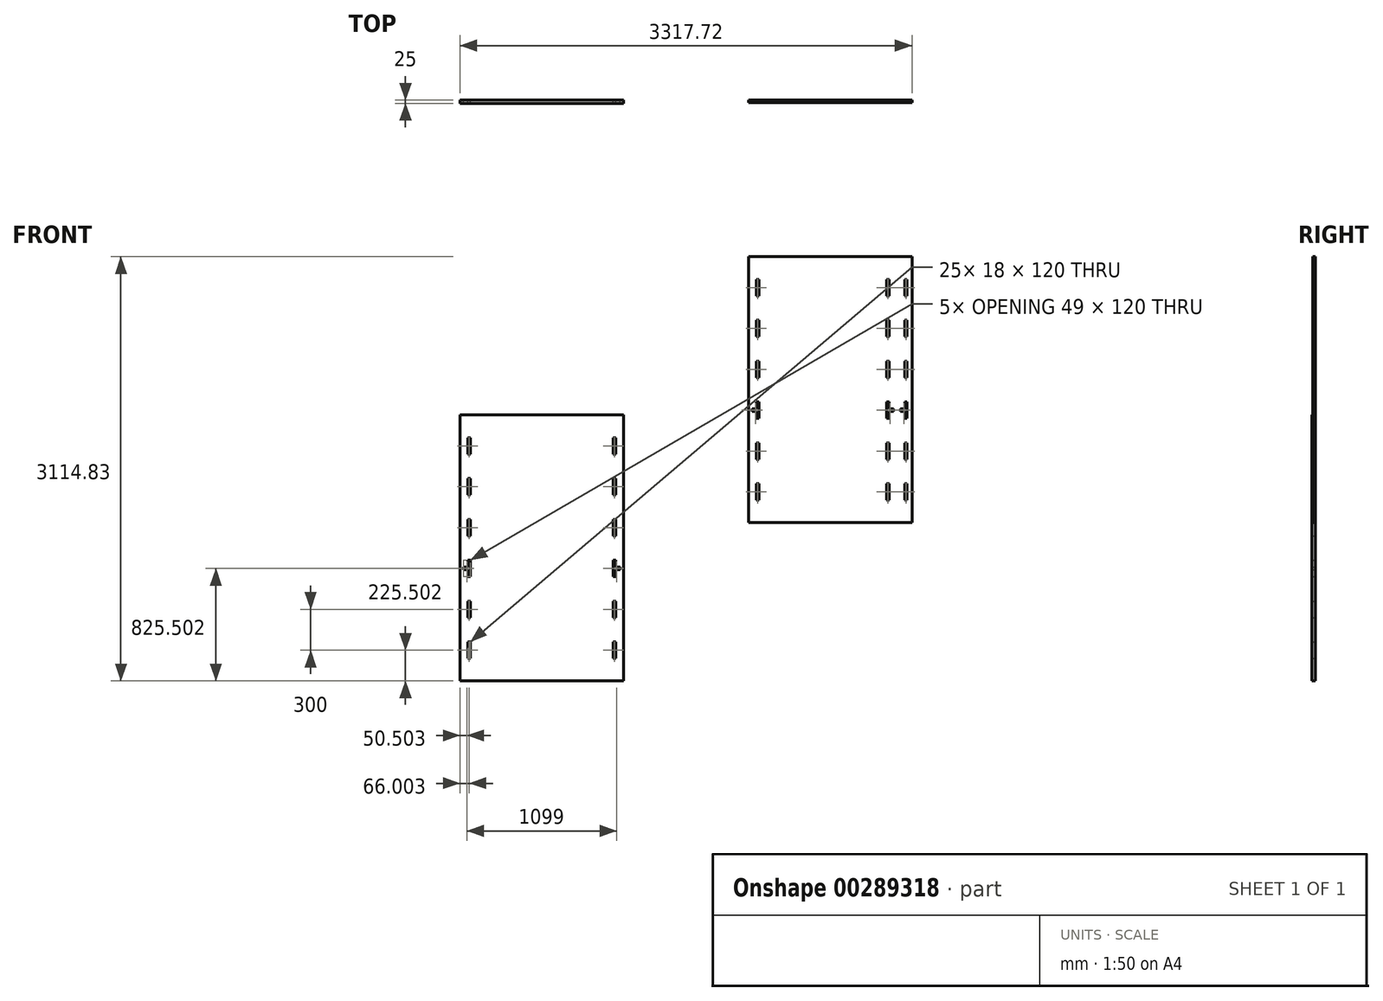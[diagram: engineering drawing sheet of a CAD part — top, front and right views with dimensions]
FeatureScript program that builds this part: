
annotation { "Feature Type Name" : "Feature", "Feature Type Description" : "" }
export const myFeature = defineFeature(function(context is Context, id is Id, definition is map)
    precondition{}
    {
        {
            var Q0;
            Q0=qCreatedBy(makeId("Front.planeOp"),FACE);
            var sketch = newSketch(context, id + "F0", { "sketchPlane" : qUnion([Q0])});
            skLineSegment(sketch, "E0.bottom", {"start": v(-15.59, 340) * mm, "end": v(15.41, 340) * mm});
            skLineSegment(sketch, "E0.top", {"start": v(-15.59, 322) * mm, "end": v(15.41, 322) * mm});
            skLineSegment(sketch, "E0.left", {"start": v(-15.59, 340) * mm, "end": v(-15.59, 322) * mm});
            skLineSegment(sketch, "E0.right", {"start": v(15.41, 340) * mm, "end": v(15.41, 322) * mm});
            skLineSegment(sketch, "E1.bottom", {"start": v(15.41, 391) * mm, "end": v(33.41, 391) * mm});
            skLineSegment(sketch, "E1.top", {"start": v(15.41, 271) * mm, "end": v(33.41, 271) * mm});
            skLineSegment(sketch, "E1.left", {"start": v(15.41, 391) * mm, "end": v(15.41, 271) * mm});
            skLineSegment(sketch, "E1.right", {"start": v(33.41, 391) * mm, "end": v(33.41, 271) * mm});
            skLineSegment(sketch, "E2", {"start": v(33.41, 331) * mm, "end": v(558.41, 331) * mm});
            skPoint(sketch, "E2.endSnap0", {"position": v(33.41, 331) * mm});
            skLineSegment(sketch, "E3", {"start": v(558.41, 331) * mm, "end": v(558.41, 369.03) * mm});
            skLineSegment(sketch, "E4.bottom", {"start": v(33.41, 571) * mm, "end": v(15.41, 571) * mm});
            skLineSegment(sketch, "E4.top", {"start": v(33.41, 691) * mm, "end": v(15.41, 691) * mm});
            skLineSegment(sketch, "E4.left", {"start": v(33.41, 571) * mm, "end": v(33.41, 691) * mm});
            skLineSegment(sketch, "E4.right", {"start": v(15.41, 571) * mm, "end": v(15.41, 691) * mm});
            skLineSegment(sketch, "E5.bottom", {"start": v(33.41, 871) * mm, "end": v(15.41, 871) * mm});
            skLineSegment(sketch, "E5.top", {"start": v(33.41, 991) * mm, "end": v(15.41, 991) * mm});
            skLineSegment(sketch, "E5.left", {"start": v(33.41, 871) * mm, "end": v(33.41, 991) * mm});
            skLineSegment(sketch, "E5.right", {"start": v(15.41, 871) * mm, "end": v(15.41, 991) * mm});
            skLineSegment(sketch, "E6.bottom", {"start": v(33.41, 1171) * mm, "end": v(15.41, 1171) * mm});
            skLineSegment(sketch, "E6.top", {"start": v(33.41, 1291) * mm, "end": v(15.41, 1291) * mm});
            skLineSegment(sketch, "E6.left", {"start": v(33.41, 1171) * mm, "end": v(33.41, 1291) * mm});
            skLineSegment(sketch, "E6.right", {"start": v(15.41, 1171) * mm, "end": v(15.41, 1291) * mm});
            skLineSegment(sketch, "E7", {"start": v(33.41, 1458) * mm, "end": v(15.41, 1458) * mm});
            skLineSegment(sketch, "E8", {"start": v(15.41, 1458) * mm, "end": v(-41.59, 1458) * mm});
            skLineSegment(sketch, "E9.bottom", {"start": v(15.41, 91) * mm, "end": v(33.41, 91) * mm});
            skLineSegment(sketch, "E9.top", {"start": v(15.41, -29) * mm, "end": v(33.41, -29) * mm});
            skLineSegment(sketch, "E9.left", {"start": v(15.41, 91) * mm, "end": v(15.41, -29) * mm});
            skLineSegment(sketch, "E9.right", {"start": v(33.41, 91) * mm, "end": v(33.41, -29) * mm});
            skLineSegment(sketch, "E10.bottom", {"start": v(15.41, -209) * mm, "end": v(33.41, -209) * mm});
            skLineSegment(sketch, "E10.top", {"start": v(15.41, -329) * mm, "end": v(33.41, -329) * mm});
            skLineSegment(sketch, "E10.left", {"start": v(15.41, -209) * mm, "end": v(15.41, -329) * mm});
            skLineSegment(sketch, "E10.right", {"start": v(33.41, -209) * mm, "end": v(33.41, -329) * mm});
            skLineSegment(sketch, "E11.bottom", {"start": v(15.41, -494.5) * mm, "end": v(33.41, -494.5) * mm});
            skLineSegment(sketch, "E12", {"start": v(69.41, -536.5) * mm, "end": v(69.41, -518.5) * mm});
            skLineSegment(sketch, "E13.MirrorCS", {"start": v(1101.41, 391) * mm, "end": v(1083.41, 391) * mm});
            skLineSegment(sketch, "E14.MirrorCS", {"start": v(1132.41, 322) * mm, "end": v(1101.41, 322) * mm});
            skLineSegment(sketch, "E15.MirrorCS", {"start": v(1101.41, -494.5) * mm, "end": v(1083.41, -494.5) * mm});
            skLineSegment(sketch, "E16.MirrorCS", {"start": v(1132.41, 340) * mm, "end": v(1101.41, 340) * mm});
            skLineSegment(sketch, "E17.MirrorCS", {"start": v(1101.41, -209) * mm, "end": v(1083.41, -209) * mm});
            skLineSegment(sketch, "E18.MirrorCS", {"start": v(1101.41, 271) * mm, "end": v(1083.41, 271) * mm});
            skLineSegment(sketch, "E19.MirrorCS", {"start": v(1101.41, 340) * mm, "end": v(1101.41, 322) * mm});
            skLineSegment(sketch, "E20.MirrorCS", {"start": v(1132.41, 340) * mm, "end": v(1132.41, 322) * mm});
            skLineSegment(sketch, "E21.MirrorCS", {"start": v(1101.41, -329) * mm, "end": v(1083.41, -329) * mm});
            skLineSegment(sketch, "E22.MirrorCS", {"start": v(1101.41, 391) * mm, "end": v(1101.41, 271) * mm});
            skLineSegment(sketch, "E23.MirrorCS", {"start": v(1083.41, 391) * mm, "end": v(1083.41, 271) * mm});
            skLineSegment(sketch, "E24.MirrorCS", {"start": v(1101.41, 91) * mm, "end": v(1101.41, -29) * mm});
            skLineSegment(sketch, "E25.MirrorCS", {"start": v(1101.41, 571) * mm, "end": v(1101.41, 691) * mm});
            skLineSegment(sketch, "E26.MirrorCS", {"start": v(1083.41, 871) * mm, "end": v(1101.41, 871) * mm});
            skLineSegment(sketch, "E27.MirrorCS", {"start": v(1083.41, 1291) * mm, "end": v(1101.41, 1291) * mm});
            skLineSegment(sketch, "E28.MirrorCS", {"start": v(1083.41, 691) * mm, "end": v(1101.41, 691) * mm});
            skLineSegment(sketch, "E29.MirrorCS", {"start": v(1101.41, 1458) * mm, "end": v(1158.41, 1458) * mm});
            skLineSegment(sketch, "E30.MirrorCS", {"start": v(1083.41, 991) * mm, "end": v(1101.41, 991) * mm});
            skLineSegment(sketch, "E31.MirrorCS", {"start": v(1101.41, -209) * mm, "end": v(1101.41, -329) * mm});
            skLineSegment(sketch, "E32.MirrorCS", {"start": v(1083.41, 571) * mm, "end": v(1101.41, 571) * mm});
            skLineSegment(sketch, "E33.MirrorCS", {"start": v(1083.41, 1458) * mm, "end": v(1101.41, 1458) * mm});
            skLineSegment(sketch, "E34.MirrorCS", {"start": v(1083.41, -209) * mm, "end": v(1083.41, -329) * mm});
            skLineSegment(sketch, "E35.MirrorCS", {"start": v(1101.41, 871) * mm, "end": v(1101.41, 991) * mm});
            skLineSegment(sketch, "E36.MirrorCS", {"start": v(1101.41, 91) * mm, "end": v(1083.41, 91) * mm});
            skLineSegment(sketch, "E37.MirrorCS", {"start": v(1101.41, 1171) * mm, "end": v(1101.41, 1291) * mm});
            skLineSegment(sketch, "E38.MirrorCS", {"start": v(1101.41, -29) * mm, "end": v(1083.41, -29) * mm});
            skLineSegment(sketch, "E39.MirrorCS", {"start": v(1083.41, 571) * mm, "end": v(1083.41, 691) * mm});
            skLineSegment(sketch, "E40.MirrorCS", {"start": v(1083.41, 1171) * mm, "end": v(1101.41, 1171) * mm});
            skLineSegment(sketch, "E41.MirrorCS", {"start": v(1083.41, 91) * mm, "end": v(1083.41, -29) * mm});
            skLineSegment(sketch, "E42.MirrorCS", {"start": v(1083.41, 1171) * mm, "end": v(1083.41, 1291) * mm});
            skLineSegment(sketch, "E43.MirrorCS", {"start": v(1083.41, 871) * mm, "end": v(1083.41, 991) * mm});
            skLineSegment(sketch, "E44.MirrorCS", {"start": v(1083.41, 331) * mm, "end": v(558.41, 331) * mm});
            skPoint(sketch, "E45.MirrorP", {"position": v(1083.41, 331) * mm});
            skLineSegment(sketch, "E46", {"start": v(1083.41, 1458) * mm, "end": v(33.41, 1458) * mm});
            skLineSegment(sketch, "E47", {"start": v(15.41, -494.5) * mm, "end": v(-41.59, -494.5) * mm});
            skLineSegment(sketch, "E48", {"start": v(33.41, -494.5) * mm, "end": v(558.41, -494.5) * mm});
            skLineSegment(sketch, "E49", {"start": v(558.41, -494.5) * mm, "end": v(1158.41, -494.5) * mm});
            skLineSegment(sketch, "E50", {"start": v(1158.41, 1458) * mm, "end": v(1158.41, -494.5) * mm});
            skLineSegment(sketch, "E51", {"start": v(-41.59, 1458) * mm, "end": v(-41.59, -494.5) * mm});
            skSolve(sketch);
        }
        {
            var Q0;
            {var subQ13=sQuery(id+"F0.wireOp",EDGE,"E0.bottom");Q0=makeQuery(id+"F0.imprint","IMPRINT",FACE,{"disambiguationData":[TD([[makeQuery(id+"F0.imprint","IMPRINT",EDGE,{"derivedFrom":subQ13}),1.0]])]});}
            extrude(context, id + "F1", {"entities" : qUnion([Q0]), "depth" : 25 * mm});
        }
        {
            var Q0;
            Q0=qCreatedBy(makeId("Front.planeOp"),FACE);
            var sketch = newSketch(context, id + "F2", { "sketchPlane" : qUnion([Q0])});
            skLineSegment(sketch, "E52.bottom", {"start": v(2102.13, 1502.33) * mm, "end": v(2133.13, 1502.33) * mm});
            skLineSegment(sketch, "E52.top", {"start": v(2102.13, 1484.33) * mm, "end": v(2133.13, 1484.33) * mm});
            skLineSegment(sketch, "E52.right", {"start": v(2133.13, 1502.33) * mm, "end": v(2133.13, 1484.33) * mm});
            skLineSegment(sketch, "E53.bottom", {"start": v(2133.13, 1553.33) * mm, "end": v(2151.13, 1553.33) * mm});
            skLineSegment(sketch, "E53.top", {"start": v(2133.13, 1433.33) * mm, "end": v(2151.13, 1433.33) * mm});
            skLineSegment(sketch, "E53.left", {"start": v(2133.13, 1553.33) * mm, "end": v(2133.13, 1433.33) * mm});
            skLineSegment(sketch, "E53.right", {"start": v(2151.13, 1553.33) * mm, "end": v(2151.13, 1433.33) * mm});
            skPoint(sketch, "E54.endSnap0", {"position": v(2151.13, 1493.33) * mm});
            skLineSegment(sketch, "E55.bottom", {"start": v(2151.13, 1733.33) * mm, "end": v(2133.13, 1733.33) * mm});
            skLineSegment(sketch, "E55.top", {"start": v(2151.13, 1853.33) * mm, "end": v(2133.13, 1853.33) * mm});
            skLineSegment(sketch, "E55.left", {"start": v(2151.13, 1733.33) * mm, "end": v(2151.13, 1853.33) * mm});
            skLineSegment(sketch, "E55.right", {"start": v(2133.13, 1733.33) * mm, "end": v(2133.13, 1853.33) * mm});
            skLineSegment(sketch, "E56.bottom", {"start": v(2151.13, 2033.33) * mm, "end": v(2133.13, 2033.33) * mm});
            skLineSegment(sketch, "E56.top", {"start": v(2151.13, 2153.33) * mm, "end": v(2133.13, 2153.33) * mm});
            skLineSegment(sketch, "E56.left", {"start": v(2151.13, 2033.33) * mm, "end": v(2151.13, 2153.33) * mm});
            skLineSegment(sketch, "E56.right", {"start": v(2133.13, 2033.33) * mm, "end": v(2133.13, 2153.33) * mm});
            skLineSegment(sketch, "E57.bottom", {"start": v(2151.13, 2333.33) * mm, "end": v(2133.13, 2333.33) * mm});
            skLineSegment(sketch, "E57.top", {"start": v(2151.13, 2453.33) * mm, "end": v(2133.13, 2453.33) * mm});
            skLineSegment(sketch, "E57.left", {"start": v(2151.13, 2333.33) * mm, "end": v(2151.13, 2453.33) * mm});
            skLineSegment(sketch, "E57.right", {"start": v(2133.13, 2333.33) * mm, "end": v(2133.13, 2453.33) * mm});
            skLineSegment(sketch, "E58.bottom", {"start": v(2133.13, 1253.33) * mm, "end": v(2151.13, 1253.33) * mm});
            skLineSegment(sketch, "E58.top", {"start": v(2133.13, 1133.33) * mm, "end": v(2151.13, 1133.33) * mm});
            skLineSegment(sketch, "E58.left", {"start": v(2133.13, 1253.33) * mm, "end": v(2133.13, 1133.33) * mm});
            skLineSegment(sketch, "E58.right", {"start": v(2151.13, 1253.33) * mm, "end": v(2151.13, 1133.33) * mm});
            skLineSegment(sketch, "E59.bottom", {"start": v(2133.13, 953.33) * mm, "end": v(2151.13, 953.33) * mm});
            skLineSegment(sketch, "E59.top", {"start": v(2133.13, 833.33) * mm, "end": v(2151.13, 833.33) * mm});
            skLineSegment(sketch, "E59.left", {"start": v(2133.13, 953.33) * mm, "end": v(2133.13, 833.33) * mm});
            skLineSegment(sketch, "E59.right", {"start": v(2151.13, 953.33) * mm, "end": v(2151.13, 833.33) * mm});
            skLineSegment(sketch, "E60.bottom", {"start": v(2133.13, 667.83) * mm, "end": v(2151.13, 667.83) * mm});
            skLineSegment(sketch, "E61", {"start": v(2102.13, 1502.33) * mm, "end": v(2102.13, 1484.33) * mm});
            skLineSegment(sketch, "E62", {"start": v(2151.13, 2620.33) * mm, "end": v(2133.13, 2620.33) * mm});
            skLineSegment(sketch, "E63", {"start": v(2133.13, 2620.33) * mm, "end": v(2076.13, 2620.33) * mm});
            skLineSegment(sketch, "E64.MirrorCS", {"start": v(3090.13, 2620.33) * mm, "end": v(3108.13, 2620.33) * mm});
            skLineSegment(sketch, "E65.MirrorCS", {"start": v(3090.13, 2453.33) * mm, "end": v(3108.13, 2453.33) * mm});
            skLineSegment(sketch, "E66.MirrorCS", {"start": v(3108.13, 2333.33) * mm, "end": v(3108.13, 2453.33) * mm});
            skLineSegment(sketch, "E67.MirrorCS", {"start": v(3090.13, 2333.33) * mm, "end": v(3108.13, 2333.33) * mm});
            skLineSegment(sketch, "E68.MirrorCS", {"start": v(3090.13, 2333.33) * mm, "end": v(3090.13, 2453.33) * mm});
            skLineSegment(sketch, "E69.MirrorCS", {"start": v(3090.13, 1733.33) * mm, "end": v(3108.13, 1733.33) * mm});
            skLineSegment(sketch, "E70.MirrorCS", {"start": v(3090.13, 2033.33) * mm, "end": v(3108.13, 2033.33) * mm});
            skLineSegment(sketch, "E71.MirrorCS", {"start": v(3090.13, 1853.33) * mm, "end": v(3108.13, 1853.33) * mm});
            skLineSegment(sketch, "E72.MirrorCS", {"start": v(3090.13, 2153.33) * mm, "end": v(3108.13, 2153.33) * mm});
            skLineSegment(sketch, "E73.MirrorCS", {"start": v(3108.13, 2033.33) * mm, "end": v(3108.13, 2153.33) * mm});
            skLineSegment(sketch, "E74.MirrorCS", {"start": v(3090.13, 1733.33) * mm, "end": v(3090.13, 1853.33) * mm});
            skLineSegment(sketch, "E75.MirrorCS", {"start": v(3108.13, 1733.33) * mm, "end": v(3108.13, 1853.33) * mm});
            skLineSegment(sketch, "E76.MirrorCS", {"start": v(3090.13, 2033.33) * mm, "end": v(3090.13, 2153.33) * mm});
            skLineSegment(sketch, "E77.MirrorCS", {"start": v(3108.13, 1433.33) * mm, "end": v(3090.13, 1433.33) * mm});
            skLineSegment(sketch, "E78.MirrorCS", {"start": v(3108.13, 1502.33) * mm, "end": v(3108.13, 1484.33) * mm});
            skLineSegment(sketch, "E79.MirrorCS", {"start": v(3108.13, 1553.33) * mm, "end": v(3090.13, 1553.33) * mm});
            skLineSegment(sketch, "E80.MirrorCS", {"start": v(3108.13, 1553.33) * mm, "end": v(3108.13, 1433.33) * mm});
            skLineSegment(sketch, "E81.MirrorCS", {"start": v(3108.13, 1133.33) * mm, "end": v(3090.13, 1133.33) * mm});
            skLineSegment(sketch, "E82.MirrorCS", {"start": v(3090.13, 1553.33) * mm, "end": v(3090.13, 1433.33) * mm});
            skLineSegment(sketch, "E83.MirrorCS", {"start": v(3108.13, 1253.33) * mm, "end": v(3090.13, 1253.33) * mm});
            skLineSegment(sketch, "E84.MirrorCS", {"start": v(3090.13, 1253.33) * mm, "end": v(3090.13, 1133.33) * mm});
            skPoint(sketch, "E85.MirrorP", {"position": v(3090.13, 1493.33) * mm});
            skLineSegment(sketch, "E86.MirrorCS", {"start": v(3108.13, 1253.33) * mm, "end": v(3108.13, 1133.33) * mm});
            skLineSegment(sketch, "E87.MirrorCS", {"start": v(3139.13, 1502.33) * mm, "end": v(3108.13, 1502.33) * mm});
            skLineSegment(sketch, "E88.MirrorCS", {"start": v(3139.13, 1502.33) * mm, "end": v(3139.13, 1484.33) * mm});
            skLineSegment(sketch, "E89.MirrorCS", {"start": v(3139.13, 1484.33) * mm, "end": v(3108.13, 1484.33) * mm});
            skLineSegment(sketch, "E90.MirrorCS", {"start": v(3108.13, 953.33) * mm, "end": v(3090.13, 953.33) * mm});
            skLineSegment(sketch, "E91.MirrorCS", {"start": v(3108.13, 833.33) * mm, "end": v(3090.13, 833.33) * mm});
            skLineSegment(sketch, "E92.MirrorCS", {"start": v(3108.13, 667.83) * mm, "end": v(3090.13, 667.83) * mm});
            skLineSegment(sketch, "E93.MirrorCS", {"start": v(3108.13, 953.33) * mm, "end": v(3108.13, 833.33) * mm});
            skLineSegment(sketch, "E94.MirrorCS", {"start": v(3090.13, 953.33) * mm, "end": v(3090.13, 833.33) * mm});
            skLineSegment(sketch, "E95.MirrorCS", {"start": v(3222.13, 1253.33) * mm, "end": v(3240.13, 1253.33) * mm});
            skLineSegment(sketch, "E96.MirrorCS", {"start": v(3222.13, 1133.33) * mm, "end": v(3240.13, 1133.33) * mm});
            skLineSegment(sketch, "E97.MirrorCS", {"start": v(3240.13, 2333.33) * mm, "end": v(3222.13, 2333.33) * mm});
            skLineSegment(sketch, "E98.MirrorCS", {"start": v(3240.13, 2033.33) * mm, "end": v(3222.13, 2033.33) * mm});
            skLineSegment(sketch, "E99.MirrorCS", {"start": v(3222.13, 1433.33) * mm, "end": v(3240.13, 1433.33) * mm});
            skLineSegment(sketch, "E100.MirrorCS", {"start": v(3222.13, 833.33) * mm, "end": v(3240.13, 833.33) * mm});
            skLineSegment(sketch, "E101.MirrorCS", {"start": v(3240.13, 2153.33) * mm, "end": v(3222.13, 2153.33) * mm});
            skLineSegment(sketch, "E102.MirrorCS", {"start": v(3222.13, 1502.33) * mm, "end": v(3222.13, 1484.33) * mm});
            skLineSegment(sketch, "E103.MirrorCS", {"start": v(3222.13, 667.83) * mm, "end": v(3240.13, 667.83) * mm});
            skLineSegment(sketch, "E104.MirrorCS", {"start": v(3222.13, 1553.33) * mm, "end": v(3240.13, 1553.33) * mm});
            skLineSegment(sketch, "E105.MirrorCS", {"start": v(3240.13, 1853.33) * mm, "end": v(3222.13, 1853.33) * mm});
            skLineSegment(sketch, "E106.MirrorCS", {"start": v(3222.13, 953.33) * mm, "end": v(3240.13, 953.33) * mm});
            skLineSegment(sketch, "E107.MirrorCS", {"start": v(3240.13, 2453.33) * mm, "end": v(3222.13, 2453.33) * mm});
            skLineSegment(sketch, "E108.MirrorCS", {"start": v(3240.13, 1733.33) * mm, "end": v(3222.13, 1733.33) * mm});
            skLineSegment(sketch, "E109.MirrorCS", {"start": v(3222.13, 1253.33) * mm, "end": v(3222.13, 1133.33) * mm});
            skLineSegment(sketch, "E110.MirrorCS", {"start": v(3240.13, 1553.33) * mm, "end": v(3240.13, 1433.33) * mm});
            skLineSegment(sketch, "E111.MirrorCS", {"start": v(3222.13, 1553.33) * mm, "end": v(3222.13, 1433.33) * mm});
            skLineSegment(sketch, "E112.MirrorCS", {"start": v(3240.13, 2620.33) * mm, "end": v(3222.13, 2620.33) * mm});
            skLineSegment(sketch, "E113.MirrorCS", {"start": v(3240.13, 1253.33) * mm, "end": v(3240.13, 1133.33) * mm});
            skLineSegment(sketch, "E114.MirrorCS", {"start": v(3240.13, 953.33) * mm, "end": v(3240.13, 833.33) * mm});
            skLineSegment(sketch, "E115.MirrorCS", {"start": v(3240.13, 2333.33) * mm, "end": v(3240.13, 2453.33) * mm});
            skLineSegment(sketch, "E116.MirrorCS", {"start": v(3240.13, 2033.33) * mm, "end": v(3240.13, 2153.33) * mm});
            skPoint(sketch, "E117.MirrorP", {"position": v(3240.13, 1493.33) * mm});
            skLineSegment(sketch, "E118.MirrorCS", {"start": v(3222.13, 2333.33) * mm, "end": v(3222.13, 2453.33) * mm});
            skLineSegment(sketch, "E119.MirrorCS", {"start": v(3222.13, 2033.33) * mm, "end": v(3222.13, 2153.33) * mm});
            skLineSegment(sketch, "E120.MirrorCS", {"start": v(3222.13, 953.33) * mm, "end": v(3222.13, 833.33) * mm});
            skLineSegment(sketch, "E121.MirrorCS", {"start": v(3222.13, 1733.33) * mm, "end": v(3222.13, 1853.33) * mm});
            skLineSegment(sketch, "E122.MirrorCS", {"start": v(3240.13, 1733.33) * mm, "end": v(3240.13, 1853.33) * mm});
            skLineSegment(sketch, "E123.MirrorCS", {"start": v(3191.13, 1502.33) * mm, "end": v(3191.13, 1484.33) * mm});
            skLineSegment(sketch, "E124.MirrorCS", {"start": v(3191.13, 1484.33) * mm, "end": v(3222.13, 1484.33) * mm});
            skLineSegment(sketch, "E125.MirrorCS", {"start": v(3191.13, 1502.33) * mm, "end": v(3222.13, 1502.33) * mm});
            skLineSegment(sketch, "E126", {"start": v(3240.13, 2620.33) * mm, "end": v(3276.13, 2620.33) * mm});
            skLineSegment(sketch, "E127", {"start": v(2076.13, 2620.33) * mm, "end": v(3276.13, 2620.33) * mm});
            skLineSegment(sketch, "E128", {"start": v(2133.13, 667.83) * mm, "end": v(2076.13, 667.83) * mm});
            skLineSegment(sketch, "E129", {"start": v(2151.13, 667.83) * mm, "end": v(3276.13, 667.83) * mm});
            skLineSegment(sketch, "E130", {"start": v(3276.13, 2620.33) * mm, "end": v(3276.13, 667.83) * mm});
            skLineSegment(sketch, "E131", {"start": v(2076.13, 2620.33) * mm, "end": v(2076.13, 667.83) * mm});
            skSolve(sketch);
        }
        {
            var Q0;
            Q0 = qSketchRegion(id + "F2", true);
            extrude(context, id + "F3", {"entities" : qUnion([Q0]), "depth" : 18 * mm});
        }
    });
